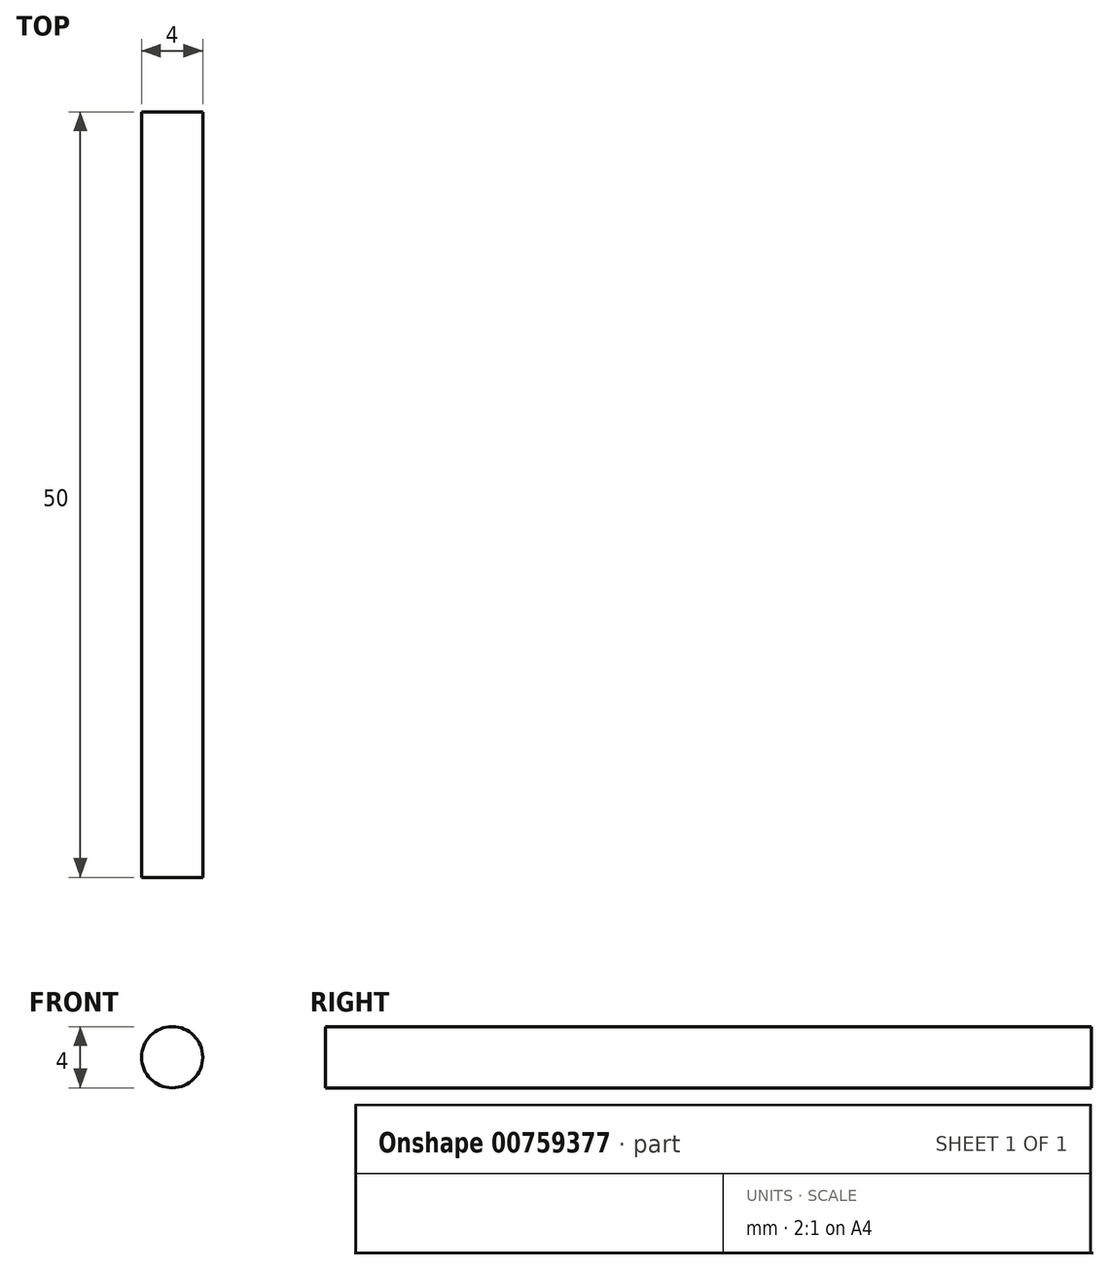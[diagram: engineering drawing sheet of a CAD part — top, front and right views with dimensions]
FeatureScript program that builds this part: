
annotation { "Feature Type Name" : "Feature", "Feature Type Description" : "" }
export const myFeature = defineFeature(function(context is Context, id is Id, definition is map)
    precondition{}
    {
        {
            var Q0;
            Q0=qCreatedBy(makeId("Front.planeOp"),FACE);
            var sketch = newSketch(context, id + "F0", { "sketchPlane" : qUnion([Q0])});
            skCircle(sketch, "E0", {"center": v(0, 0) * mm, "radius": 2 * mm});
            skSolve(sketch);
        }
        {
            var Q0;
            Q0=makeQuery(id+"F0.imprint","IMPRINT",FACE,{"disambiguationData":[TD([[makeQuery(id+"F0.imprint","IMPRINT",EDGE,{"derivedFrom":sQuery(id+"F0.wireOp",EDGE,"E0")}),1.0]])]});
            extrude(context, id + "F1", {"entities" : qUnion([Q0]), "oppositeDirection" : true, "depth" : 50 * mm, "offsetDistance" : 25 * mm});
        }
    });
